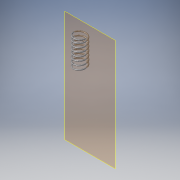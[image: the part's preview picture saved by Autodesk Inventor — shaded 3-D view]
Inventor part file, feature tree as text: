
AUTODESK INVENTOR PART (.ipt)
format: ipt  version: 2016 (Build 200138000, 138)  size: 427,008 bytes
history: native  units: in
note: dims shown in document units (in); Inventor stores cm internally (conversion verified against a paired STEP export)
features: reference x2, plane x1, helix x1, sketch x1
ambient origin geometry x8: Origin, YZ Plane, XZ Plane, XY Plane, X Axis, Y Axis, Z Axis, Center Point
bodies: Solid1 (feature_tree)
feature tree (5):
  plane  "Work Plane1"
  helix  "Coil1"  [1 undecoded]
  sketch  "Sketch1"  dims[d1=0.08in d2=1.0in d3=1.0in d4=0.92in d5=2.7559in d6=0.0in d7=90.0deg d8=90.0deg d9=0.0in d10=0.0in]
  reference  "Reference1"
  reference  "Reference2"
note: 1 required parameter value undecoded (feature->parameter linkage not recoverable at this tier; creation-order binding heuristic only, values carry confidence <= 0.55)
